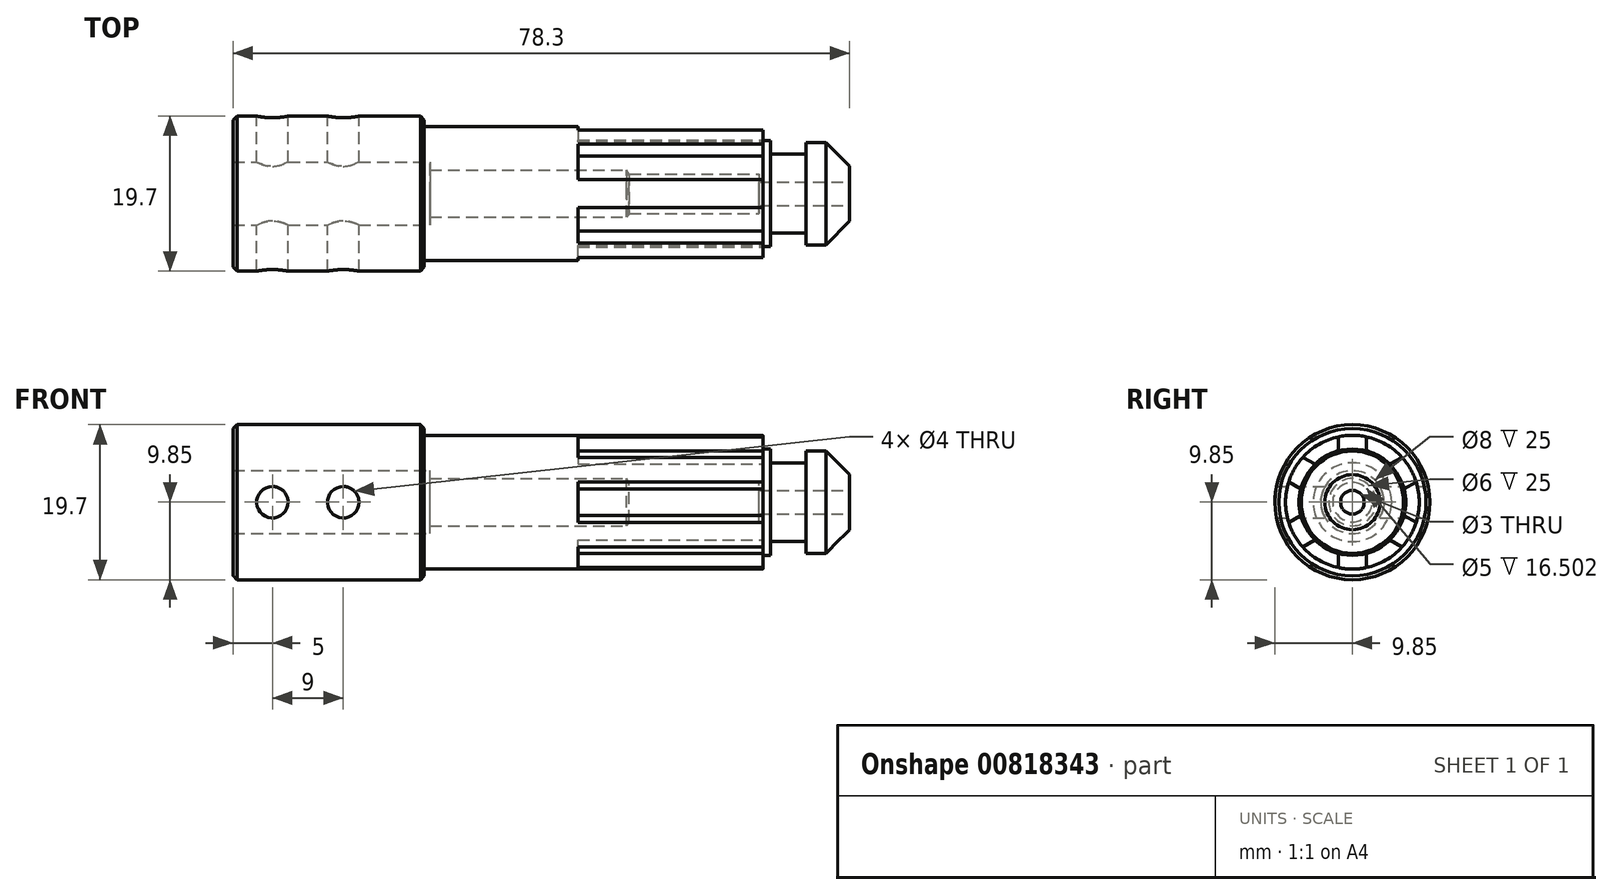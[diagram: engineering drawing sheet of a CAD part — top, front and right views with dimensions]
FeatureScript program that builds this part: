
annotation { "Feature Type Name" : "Feature", "Feature Type Description" : "" }
export const myFeature = defineFeature(function(context is Context, id is Id, definition is map)
    precondition{}
    {
        {
            var Q0;
            Q0=qCreatedBy(makeId("Front.planeOp"),FACE);
            var sketch = newSketch(context, id + "F0", { "sketchPlane" : qUnion([Q0])});
            skLineSegment(sketch, "E0", {"start": v(0, 0) * mm, "end": v(0, 9.85) * mm});
            skLineSegment(sketch, "E1", {"start": v(0, 9.85) * mm, "end": v(24.3, 9.85) * mm});
            skLineSegment(sketch, "E2", {"start": v(24.3, 9.85) * mm, "end": v(24.3, 8.5) * mm});
            skLineSegment(sketch, "E3", {"start": v(24.3, 8.5) * mm, "end": v(44.3, 8.5) * mm});
            skLineSegment(sketch, "E4", {"start": v(44.3, 8.5) * mm, "end": v(44.3, 8.5) * mm});
            skLineSegment(sketch, "E5", {"start": v(44.3, 8.5) * mm, "end": v(67.3, 8.5) * mm});
            skLineSegment(sketch, "E6", {"start": v(67.3, 8.5) * mm, "end": v(67.3, 6.75) * mm});
            skLineSegment(sketch, "E7", {"start": v(67.3, 6.75) * mm, "end": v(68.3, 6.75) * mm});
            skLineSegment(sketch, "E8", {"start": v(68.3, 6.75) * mm, "end": v(68.3, 5) * mm});
            skLineSegment(sketch, "E9", {"start": v(68.3, 5) * mm, "end": v(72.8, 5) * mm});
            skLineSegment(sketch, "E10", {"start": v(72.8, 5) * mm, "end": v(72.8, 6.5) * mm});
            skLineSegment(sketch, "E11", {"start": v(72.8, 6.5) * mm, "end": v(75.3, 6.5) * mm});
            skLineSegment(sketch, "E12", {"start": v(75.3, 6.5) * mm, "end": v(78.3, 3.5) * mm});
            skLineSegment(sketch, "E13", {"start": v(78.3, 3.5) * mm, "end": v(78.3, 0) * mm});
            skLineSegment(sketch, "E14", {"start": v(78.3, 0) * mm, "end": v(0, 0) * mm});
            skSolve(sketch);
        }
        {
            var Q0;
            Q0=makeQuery(id+"F0.imprint","IMPRINT",FACE,{"disambiguationData":[TD([[makeQuery(id+"F0.imprint","IMPRINT",EDGE,{"derivedFrom":sQuery(id+"F0.wireOp",EDGE,"E0")}),-1.0]])]});
            var Q1;
            Q1=sQuery(id+"F0.wireOp",EDGE,"E14");
            revolve(context, id + "F1", {"surfaceOperationType" : NewSurfaceOperationType.NEW, "entities" : qUnion([Q0]), "axis" : qUnion([Q1]), "revolveType" : RevolveType.FULL});
        }
        {
            var Q0;
            Q0=makeQuery(id+"F1.opRevolve","SWEPT_FACE",FACE,{"disambiguationData":[OSD([sQuery(id+"F0.wireOp",EDGE,"E0")])]});
            var sketch = newSketch(context, id + "F2", { "sketchPlane" : qUnion([Q0])});
            skPoint(sketch, "E15", {"position": v(0, 0) * mm});
            skSolve(sketch);
        }
        {
            var Q0;
            Q0=sQuery(id+"F2.wireOp",VERTEX,"E15");
            var Q1;
            Q1=makeQuery(id+"F1.opRevolve","SWEPT_BODY",BODY,{"disambiguationData":[OSD([sQuery(id+"F0.wireOp",EDGE,"E0"),sQuery(id+"F0.wireOp",EDGE,"E1"),sQuery(id+"F0.wireOp",EDGE,"E2"),sQuery(id+"F0.wireOp",EDGE,"E3"),sQuery(id+"F0.wireOp",EDGE,"E5"),sQuery(id+"F0.wireOp",EDGE,"E6"),sQuery(id+"F0.wireOp",EDGE,"E7"),sQuery(id+"F0.wireOp",EDGE,"E8"),sQuery(id+"F0.wireOp",EDGE,"E9"),sQuery(id+"F0.wireOp",EDGE,"E10"),sQuery(id+"F0.wireOp",EDGE,"E11"),sQuery(id+"F0.wireOp",EDGE,"E12"),sQuery(id+"F0.wireOp",EDGE,"E13"),sQuery(id+"F0.wireOp",EDGE,"E14")])]});
            hole(context, id + "F3", {"style" : HoleStyle.C_BORE, "endStyle" : HoleEndStyle.BLIND, "holeDiameter" : 6 * mm, "cBoreDiameter" : 8 * mm, "cBoreDepth" : 25 * mm, "majorDiameter" : 5 * mm, "holeDepth" : 50 * mm, "isTappedThrough" : true, "tappedDepth" : 12 * mm, "tapClearance" : 3, "locations" : qUnion([Q0]), "scope" : qUnion([Q1])});
        }
        {
            var Q0;
            Q0=sQuery(id+"F2.wireOp",VERTEX,"E15");
            var Q1;
            Q1=makeQuery(id+"F1.opRevolve","SWEPT_BODY",BODY,{"disambiguationData":[OSD([sQuery(id+"F0.wireOp",EDGE,"E0"),sQuery(id+"F0.wireOp",EDGE,"E1"),sQuery(id+"F0.wireOp",EDGE,"E2"),sQuery(id+"F0.wireOp",EDGE,"E3"),sQuery(id+"F0.wireOp",EDGE,"E5"),sQuery(id+"F0.wireOp",EDGE,"E6"),sQuery(id+"F0.wireOp",EDGE,"E7"),sQuery(id+"F0.wireOp",EDGE,"E8"),sQuery(id+"F0.wireOp",EDGE,"E9"),sQuery(id+"F0.wireOp",EDGE,"E10"),sQuery(id+"F0.wireOp",EDGE,"E11"),sQuery(id+"F0.wireOp",EDGE,"E12"),sQuery(id+"F0.wireOp",EDGE,"E13"),sQuery(id+"F0.wireOp",EDGE,"E14")])]});
            hole(context, id + "F4", {"style" : HoleStyle.C_BORE, "endStyle" : HoleEndStyle.THROUGH, "holeDiameter" : 3 * mm, "cBoreDiameter" : 5 * mm, "cBoreDepth" : 15 * mm, "majorDiameter" : 5 * mm, "isTappedThrough" : true, "tappedDepth" : 12 * mm, "tapClearance" : 3, "locations" : qUnion([Q0]), "scope" : qUnion([Q1])});
        }
        {
            var Q0;
            Q0=makeQuery(id+"F1.opRevolve","SWEPT_FACE",FACE,{"disambiguationData":[OSD([sQuery(id+"F0.wireOp",EDGE,"E6")])]});
            var sketch = newSketch(context, id + "F5", { "sketchPlane" : qUnion([Q0])});
            skLineSegment(sketch, "E16", {"start": v(-1.8, 11.46) * mm, "end": v(-1.8, 6.54) * mm});
            skLineSegment(sketch, "E17", {"start": v(1.8, 11.46) * mm, "end": v(1.8, 6.54) * mm});
            skLineSegment(sketch, "E18.1.0", {"start": v(-10.83, 4.17) * mm, "end": v(-6.56, 1.7) * mm});
            skLineSegment(sketch, "E18.2.0", {"start": v(-9.03, -7.29) * mm, "end": v(-4.76, -4.83) * mm});
            skPoint(sketch, "E18.center", {"position": v(0, 0) * mm});
            skLineSegment(sketch, "E19.2.3.0", {"start": v(1.8, -11.46) * mm, "end": v(1.8, -6.54) * mm});
            skLineSegment(sketch, "E19.2.4.0", {"start": v(10.83, -4.17) * mm, "end": v(6.56, -1.7) * mm});
            skLineSegment(sketch, "E19.2.5.0", {"start": v(9.03, 7.29) * mm, "end": v(4.76, 4.83) * mm});
            skLineSegment(sketch, "E20.1.0", {"start": v(-7.76, 6.56) * mm, "end": v(-4.76, 4.83) * mm});
            skLineSegment(sketch, "E20.2.0", {"start": v(-9.56, -3.44) * mm, "end": v(-6.56, -1.7) * mm});
            skLineSegment(sketch, "E20.3.0", {"start": v(-1.8, -10) * mm, "end": v(-1.8, -6.54) * mm});
            skLineSegment(sketch, "E20.4.0", {"start": v(7.76, -6.56) * mm, "end": v(4.76, -4.83) * mm});
            skLineSegment(sketch, "E20.5.0", {"start": v(9.56, 3.44) * mm, "end": v(6.56, 1.7) * mm});
            skArc(sketch, "E21", {"start": v(-1.8, 6.54) * mm, "mid": v(-3.4, 5.87) * mm, "end": v(-4.76, 4.83) * mm});
            skLineSegment(sketch, "E22", {"start": v(-7.76, 6.56) * mm, "end": v(-1.8, 11.46) * mm});
            skLineSegment(sketch, "E23", {"start": v(1.8, 11.46) * mm, "end": v(9.03, 7.29) * mm});
            skLineSegment(sketch, "E24", {"start": v(-10.83, 4.17) * mm, "end": v(-9.56, -3.44) * mm});
            skArc(sketch, "E25.trimOffspring", {"start": v(-6.56, 1.7) * mm, "mid": v(-6.78, 0) * mm, "end": v(-6.56, -1.7) * mm});
            skArc(sketch, "E26.trimOffspring", {"start": v(-4.76, -4.83) * mm, "mid": v(-3.4, -5.87) * mm, "end": v(-1.8, -6.54) * mm});
            skArc(sketch, "E27.trimOffspring", {"start": v(1.8, -6.54) * mm, "mid": v(3.39, -5.87) * mm, "end": v(4.76, -4.83) * mm});
            skArc(sketch, "E28.trimOffspring", {"start": v(6.56, -1.7) * mm, "mid": v(6.78, 0) * mm, "end": v(6.56, 1.7) * mm});
            skArc(sketch, "E29.trimOffspring", {"start": v(4.76, 4.83) * mm, "mid": v(3.4, 5.87) * mm, "end": v(1.8, 6.54) * mm});
            skLineSegment(sketch, "E30", {"start": v(-9.03, -7.29) * mm, "end": v(-1.8, -10) * mm});
            skLineSegment(sketch, "E31", {"start": v(1.8, -11.46) * mm, "end": v(7.76, -6.56) * mm});
            skLineSegment(sketch, "E32", {"start": v(10.83, -4.17) * mm, "end": v(9.56, 3.44) * mm});
            skSolve(sketch);
        }
        {
            var Q0;
            {var subQ0=sQuery(id+"F5.wireOp",EDGE,"E21");Q0=makeQuery(id+"F5.imprint","IMPRINT",FACE,{"disambiguationData":[TD([[makeQuery(id+"F5.imprint","IMPRINT",EDGE,{"derivedFrom":subQ0}),-1.0]])]});}
            var Q1;
            {var subQ0=sQuery(id+"F5.wireOp",EDGE,"E25.trimOffspring");Q1=makeQuery(id+"F5.imprint","IMPRINT",FACE,{"disambiguationData":[TD([[makeQuery(id+"F5.imprint","IMPRINT",EDGE,{"derivedFrom":subQ0}),-1.0]])]});}
            var Q2;
            {var subQ0=sQuery(id+"F5.wireOp",EDGE,"E26.trimOffspring");Q2=makeQuery(id+"F5.imprint","IMPRINT",FACE,{"disambiguationData":[TD([[makeQuery(id+"F5.imprint","IMPRINT",EDGE,{"derivedFrom":subQ0}),-1.0]])]});}
            var Q3;
            {var subQ0=sQuery(id+"F5.wireOp",EDGE,"E29.trimOffspring");Q3=makeQuery(id+"F5.imprint","IMPRINT",FACE,{"disambiguationData":[TD([[makeQuery(id+"F5.imprint","IMPRINT",EDGE,{"derivedFrom":subQ0}),-1.0]])]});}
            var Q4;
            {var subQ0=sQuery(id+"F5.wireOp",EDGE,"E28.trimOffspring");Q4=makeQuery(id+"F5.imprint","IMPRINT",FACE,{"disambiguationData":[TD([[makeQuery(id+"F5.imprint","IMPRINT",EDGE,{"derivedFrom":subQ0}),-1.0]])]});}
            var Q5;
            {var subQ0=sQuery(id+"F5.wireOp",EDGE,"E27.trimOffspring");Q5=makeQuery(id+"F5.imprint","IMPRINT",FACE,{"disambiguationData":[TD([[makeQuery(id+"F5.imprint","IMPRINT",EDGE,{"derivedFrom":subQ0}),-1.0]])]});}
            extrude(context, id + "F6", {"entities" : qUnion([Q0, Q1, Q2, Q3, Q4, Q5]), "operationType" : NewBodyOperationType.REMOVE, "oppositeDirection" : true, "depth" : 23.5 * mm, "offsetDistance" : 25 * mm});
        }
        {
            var Q0;
            Q0=qCreatedBy(makeId("Front.planeOp"),FACE);
            cPlane(context, id + "F7", {"entities" : qUnion([Q0]), "cplaneType" : CPlaneType.OFFSET, "offset" : 25 * mm, "width" : 150 * mm, "height" : 150 * mm});
        }
        {
            var Q0;
            Q0=qCreatedBy(id+"F7.planeOp",FACE);
            var sketch = newSketch(context, id + "F8", { "sketchPlane" : qUnion([Q0])});
            skPoint(sketch, "E33", {"position": v(5, 0) * mm});
            skPoint(sketch, "E34", {"position": v(14, 0) * mm});
            skSolve(sketch);
        }
        {
            var Q0;
            Q0=sQuery(id+"F8.wireOp",VERTEX,"E33");
            var Q1;
            Q1=sQuery(id+"F8.wireOp",VERTEX,"E34");
            var Q2;
            Q2=makeQuery(id+"F1.opRevolve","SWEPT_BODY",BODY,{"disambiguationData":[OSD([sQuery(id+"F0.wireOp",EDGE,"E0"),sQuery(id+"F0.wireOp",EDGE,"E1"),sQuery(id+"F0.wireOp",EDGE,"E2"),sQuery(id+"F0.wireOp",EDGE,"E3"),sQuery(id+"F0.wireOp",EDGE,"E5"),sQuery(id+"F0.wireOp",EDGE,"E6"),sQuery(id+"F0.wireOp",EDGE,"E7"),sQuery(id+"F0.wireOp",EDGE,"E8"),sQuery(id+"F0.wireOp",EDGE,"E9"),sQuery(id+"F0.wireOp",EDGE,"E10"),sQuery(id+"F0.wireOp",EDGE,"E11"),sQuery(id+"F0.wireOp",EDGE,"E12"),sQuery(id+"F0.wireOp",EDGE,"E13"),sQuery(id+"F0.wireOp",EDGE,"E14")])]});
            hole(context, id + "F9", {"style" : HoleStyle.SIMPLE, "endStyle" : HoleEndStyle.THROUGH, "holeDiameter" : 4 * mm, "majorDiameter" : 5 * mm, "isTappedThrough" : true, "tappedDepth" : 12 * mm, "tapClearance" : 3, "locations" : qUnion([Q0, Q1]), "scope" : qUnion([Q2])});
        }
        {
            var Q0;
            Q0=makeQuery(id+"F9.hole-0.boolean.opBoolean","INTERSECT",EDGE,{"disambiguationData":[OD(0.0)],"derivedFrom":[makeQuery(id+"F1.opRevolve","SWEPT_FACE",FACE,{"disambiguationData":[OSD([sQuery(id+"F0.wireOp",EDGE,"E1")])]}),makeQuery(id+"F9.hole-0.opRevolve","SWEPT_FACE",FACE,{"disambiguationData":[OSD([sQuery(id+"F9.hole-0.sketch.wireOp",EDGE,"core_line_2")])]})]});
            var Q1;
            Q1=makeQuery(id+"F9.hole-1.boolean.opBoolean","INTERSECT",EDGE,{"disambiguationData":[OD(0.0)],"derivedFrom":[makeQuery(id+"F1.opRevolve","SWEPT_FACE",FACE,{"disambiguationData":[OSD([sQuery(id+"F0.wireOp",EDGE,"E1")])]}),makeQuery(id+"F9.hole-1.opRevolve","SWEPT_FACE",FACE,{"disambiguationData":[OSD([sQuery(id+"F9.hole-1.sketch.wireOp",EDGE,"core_line_2")])]})]});
            var Q2;
            Q2=makeQuery(id+"F9.hole-1.boolean.opBoolean","INTERSECT",EDGE,{"disambiguationData":[OD(1.0)],"derivedFrom":[makeQuery(id+"F1.opRevolve","SWEPT_FACE",FACE,{"disambiguationData":[OSD([sQuery(id+"F0.wireOp",EDGE,"E1")])]}),makeQuery(id+"F9.hole-1.opRevolve","SWEPT_FACE",FACE,{"disambiguationData":[OSD([sQuery(id+"F9.hole-1.sketch.wireOp",EDGE,"core_line_2")])]})]});
            var Q3;
            Q3=makeQuery(id+"F9.hole-0.boolean.opBoolean","INTERSECT",EDGE,{"disambiguationData":[OD(1.0)],"derivedFrom":[makeQuery(id+"F1.opRevolve","SWEPT_FACE",FACE,{"disambiguationData":[OSD([sQuery(id+"F0.wireOp",EDGE,"E1")])]}),makeQuery(id+"F9.hole-0.opRevolve","SWEPT_FACE",FACE,{"disambiguationData":[OSD([sQuery(id+"F9.hole-0.sketch.wireOp",EDGE,"core_line_2")])]})]});
            var Q4;
            Q4=makeQuery(id+"F3.hole-0.boolean.opBoolean","COPY",EDGE,{"derivedFrom":makeQuery(id+"F3.hole-0.opRevolve","SWEPT_EDGE",EDGE,{"disambiguationData":[OSD([sQuery(id+"F3.hole-0.sketch.wireOp",EDGE,"cbore_start_line_2"),sQuery(id+"F3.hole-0.sketch.wireOp",EDGE,"cbore_start_line_3")])]})});
            var Q5;
            Q5=makeQuery(id+"F1.opRevolve","SWEPT_EDGE",EDGE,{"disambiguationData":[OSD([sQuery(id+"F0.wireOp",EDGE,"E0"),sQuery(id+"F0.wireOp",EDGE,"E1")])]});
            var Q6;
            Q6=makeQuery(id+"F1.opRevolve","SWEPT_EDGE",EDGE,{"disambiguationData":[OSD([sQuery(id+"F0.wireOp",EDGE,"E1"),sQuery(id+"F0.wireOp",EDGE,"E2")])]});
            var Q7;
            Q7=makeQuery(id+"F4.hole-0.boolean.opBoolean","INTERSECT",EDGE,{"derivedFrom":[makeQuery(id+"F1.opRevolve","SWEPT_FACE",FACE,{"disambiguationData":[OSD([sQuery(id+"F0.wireOp",EDGE,"E13")])]}),makeQuery(id+"F4.hole-0.opRevolve","SWEPT_FACE",FACE,{"disambiguationData":[OSD([sQuery(id+"F4.hole-0.sketch.wireOp",EDGE,"core_line_2")])]})]});
            chamfer(context, id + "F10", {"entities" : qUnion([Q0, Q1, Q2, Q3, Q4, Q5, Q6, Q7]), "width" : .5 * mm});
        }
    });
